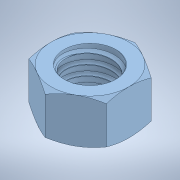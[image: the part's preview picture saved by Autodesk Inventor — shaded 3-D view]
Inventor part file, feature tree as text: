
AUTODESK INVENTOR PART (.ipt)
format: ipt  version: 2021 (Build 250183000, 183)  size: 283,136 bytes
history: native  units: in
note: dims shown in document units (in); Inventor stores cm internally (conversion verified against a paired STEP export)
features: mirror x1
ambient origin geometry x8: Origin, YZ Plane, XZ Plane, XY Plane, X Axis, Y Axis, Z Axis, Center Point
bodies: Solid1 (feature_tree)
feature tree (1):
  mirror  "Mirror1"
